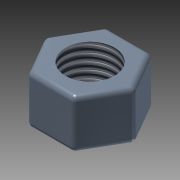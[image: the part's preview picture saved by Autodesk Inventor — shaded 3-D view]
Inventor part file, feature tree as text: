
AUTODESK INVENTOR PART (.ipt)
format: ipt  version: 2015 (Build 190159000, 159)  size: 128,512 bytes
history: native  units: mm
features: extrude x1, thread x1, fillet x1, sketch x1
ambient origin geometry x8: Origin, YZ Plane, XZ Plane, XY Plane, X Axis, Y Axis, Z Axis, Center Point
bodies: 实体1 (feature_tree)
feature tree (4):
  extrude  "拉伸1"  Depth=10.0mm
  thread  "螺纹1"  [1 undecoded]
  fillet  "圆角1"  Radius=10.0mm
  sketch  "草图1"  dims[d0=16.0mm d1=10.0mm d2=10.0mm d3=0.0mm d4=10.0mm d5=0.0mm d6=1.0mm]
note: 1 required parameter value undecoded (feature->parameter linkage not recoverable at this tier; creation-order binding heuristic only, values carry confidence <= 0.55)
